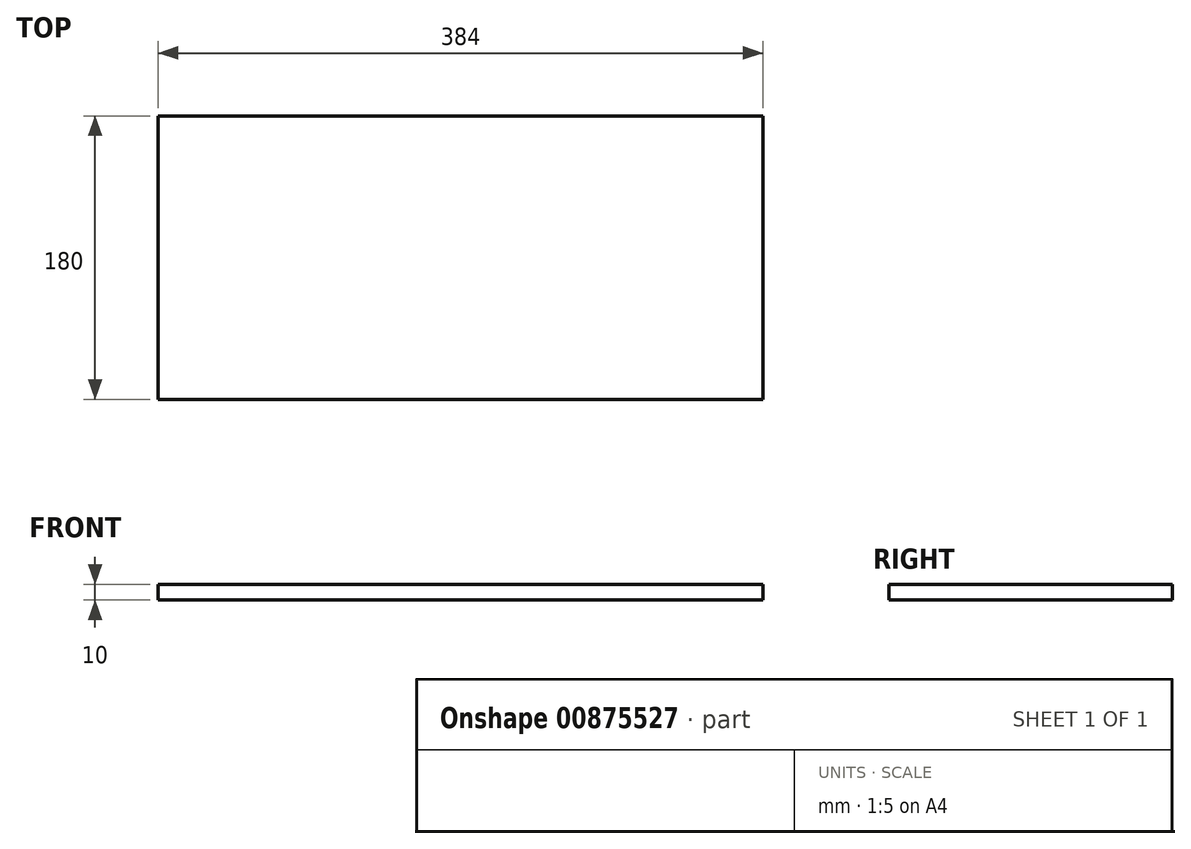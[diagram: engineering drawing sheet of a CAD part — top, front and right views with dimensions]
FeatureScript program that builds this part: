
annotation { "Feature Type Name" : "Feature", "Feature Type Description" : "" }
export const myFeature = defineFeature(function(context is Context, id is Id, definition is map)
    precondition{}
    {
        {
            var Q0;
            Q0=qCreatedBy(makeId("Top.planeOp"),FACE);
            var sketch = newSketch(context, id + "F0", { "sketchPlane" : qUnion([Q0])});
            skLineSegment(sketch, "E0.bottom", {"start": v(-179.8, 10.26) * mm, "end": v(204.2, 10.26) * mm});
            skLineSegment(sketch, "E0.top", {"start": v(-179.8, -169.74) * mm, "end": v(204.2, -169.74) * mm});
            skLineSegment(sketch, "E0.left", {"start": v(-179.8, 10.26) * mm, "end": v(-179.8, -169.74) * mm});
            skLineSegment(sketch, "E0.right", {"start": v(204.2, 10.26) * mm, "end": v(204.2, -169.74) * mm});
            skSolve(sketch);
        }
        {
            var Q0;
            Q0=makeQuery(id+"F0.imprint","IMPRINT",FACE,{"disambiguationData":[TD([[makeQuery(id+"F0.imprint","IMPRINT",EDGE,{"derivedFrom":sQuery(id+"F0.wireOp",EDGE,"E0.bottom")}),-1.0]])]});
            extrude(context, id + "F1", {"entities" : qUnion([Q0]), "depth" : 10 * mm, "offsetDistance" : 25 * mm});
        }
    });
